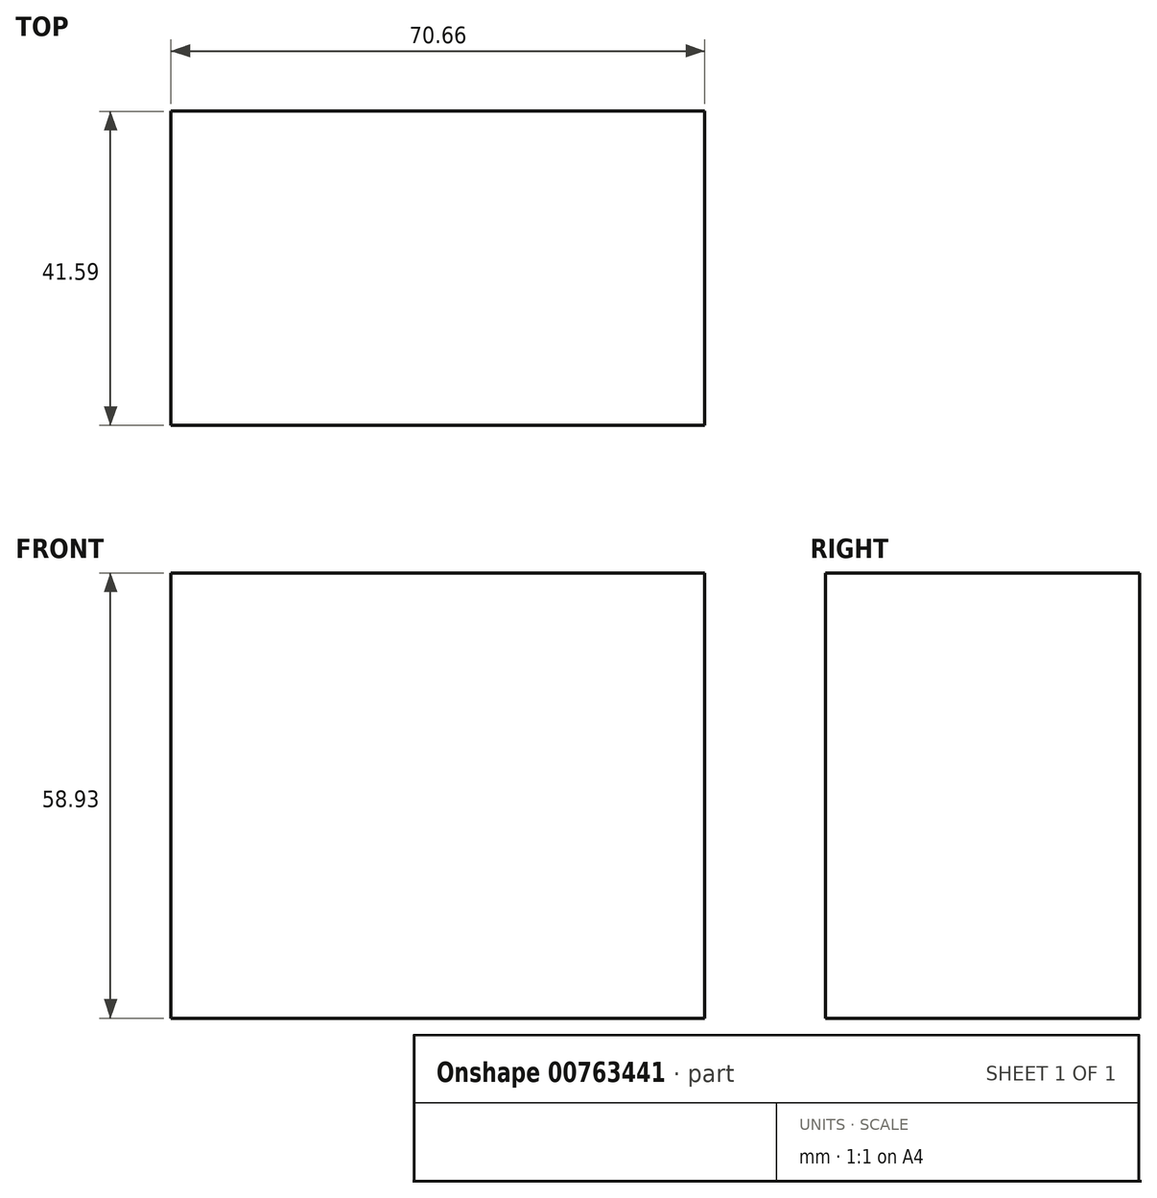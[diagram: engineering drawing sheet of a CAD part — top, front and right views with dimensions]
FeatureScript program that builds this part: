
annotation { "Feature Type Name" : "Feature", "Feature Type Description" : "" }
export const myFeature = defineFeature(function(context is Context, id is Id, definition is map)
    precondition{}
    {
        {
            var Q0;
            Q0=qCreatedBy(makeId("Top.planeOp"),FACE);
            var sketch = newSketch(context, id + "F0", { "sketchPlane" : qUnion([Q0])});
            skLineSegment(sketch, "E0.bottom", {"start": v(-55.45, 61.64) * mm, "end": v(15.21, 61.64) * mm});
            skLineSegment(sketch, "E0.top", {"start": v(-55.45, 20.05) * mm, "end": v(15.21, 20.05) * mm});
            skLineSegment(sketch, "E0.left", {"start": v(-55.45, 61.64) * mm, "end": v(-55.45, 20.05) * mm});
            skLineSegment(sketch, "E0.right", {"start": v(15.21, 61.64) * mm, "end": v(15.21, 20.05) * mm});
            skSolve(sketch);
        }
        {
            var Q0;
            Q0=makeQuery(id+"F0.imprint","IMPRINT",FACE,{"disambiguationData":[TD([[makeQuery(id+"F0.imprint","IMPRINT",EDGE,{"derivedFrom":sQuery(id+"F0.wireOp",EDGE,"E0.bottom")}),-1.0]])]});
            extrude(context, id + "F1", {"entities" : qUnion([Q0]), "depth" : 58.93 * mm, "offsetDistance" : 25.4 * mm});
        }
    });
